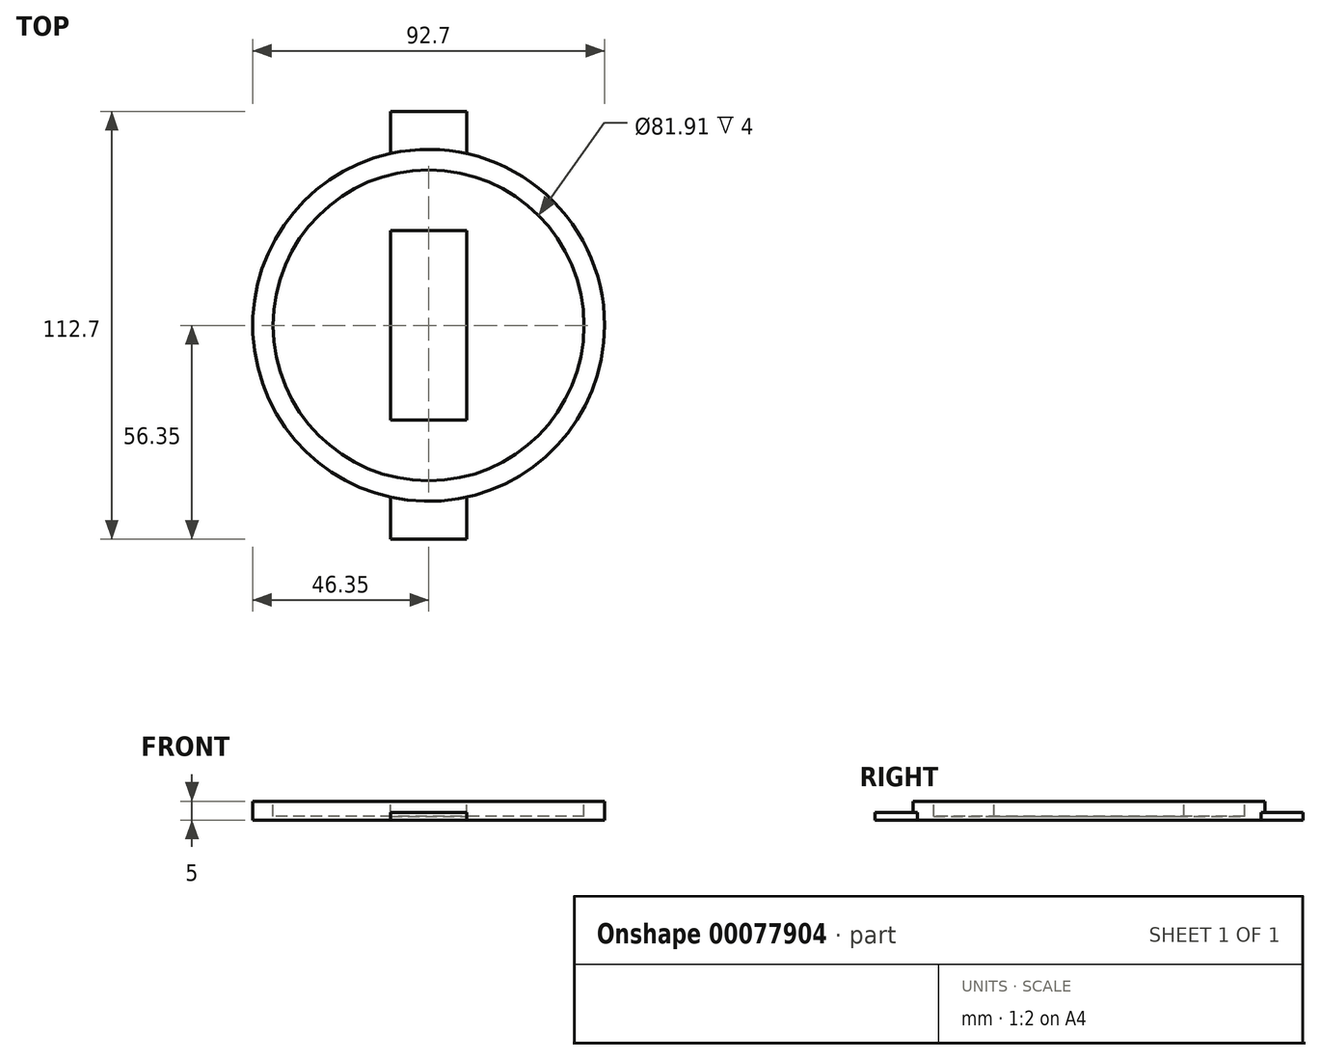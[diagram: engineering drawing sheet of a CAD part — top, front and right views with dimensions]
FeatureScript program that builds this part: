
annotation { "Feature Type Name" : "Feature", "Feature Type Description" : "" }
export const myFeature = defineFeature(function(context is Context, id is Id, definition is map)
    precondition{}
    {
        {
            var Q0;
            Q0=qCreatedBy(makeId("Top.planeOp"),FACE);
            var sketch = newSketch(context, id + "F0", { "sketchPlane" : qUnion([Q0])});
            skCircle(sketch, "E0", {"center": v(0, 0) * mm, "radius": 46.35 * mm});
            skLineSegment(sketch, "E1.bottom", {"start": v(60, -60) * mm, "end": v(-60, -60) * mm});
            skLineSegment(sketch, "E1.top", {"start": v(60, 60) * mm, "end": v(-60, 60) * mm});
            skLineSegment(sketch, "E1.left", {"start": v(60, -60) * mm, "end": v(60, 60) * mm});
            skLineSegment(sketch, "E1.right", {"start": v(-60, -60) * mm, "end": v(-60, 60) * mm});
            skSolve(sketch);
        }
        {
            var Q0;
            Q0=makeQuery(id+"F0.imprint","IMPRINT",FACE,{"disambiguationData":[TD([[makeQuery(id+"F0.imprint","IMPRINT",EDGE,{"derivedFrom":sQuery(id+"F0.wireOp",EDGE,"E0")}),1.0]])]});
            var Q1;
            Q1=makeQuery(id+"F0.imprint","IMPRINT",FACE,{"disambiguationData":[TD([[makeQuery(id+"F0.imprint","IMPRINT",EDGE,{"derivedFrom":sQuery(id+"F0.wireOp",EDGE,"da6a9297-29b8-4a20-b414-be6ac6d7b623.bottom")}),1.0]])]});
            extrude(context, id + "F1", {"entities" : qUnion([Q0, Q1]), "depth" : 5 * mm});
        }
        {
            var Q0;
            Q0=makeQuery(id+"F1.opExtrude","CAP_FACE",FACE,{"disambiguationData":[OSD([sQuery(id+"F0.wireOp",EDGE,"E0")])],"isStart":false});
            var sketch = newSketch(context, id + "F2", { "sketchPlane" : qUnion([Q0])});
            skLineSegment(sketch, "E2.bottom", {"start": v(-10, -25) * mm, "end": v(10, -25) * mm});
            skLineSegment(sketch, "E2.top", {"start": v(-10, 25) * mm, "end": v(10, 25) * mm});
            skLineSegment(sketch, "E2.left", {"start": v(-10, -25) * mm, "end": v(-10, 25) * mm});
            skLineSegment(sketch, "E2.right", {"start": v(10, -25) * mm, "end": v(10, 25) * mm});
            skPoint(sketch, "E2.middle", {"position": v(0, 0) * mm});
            skCircle(sketch, "E3", {"center": v(0, 0) * mm, "radius": 40.95 * mm});
            skSolve(sketch);
        }
        {
            var Q0;
            Q0=makeQuery(id+"F2.imprint","IMPRINT",FACE,{"disambiguationData":[TD([[makeQuery(id+"F2.imprint","IMPRINT",EDGE,{"derivedFrom":sQuery(id+"F2.wireOp",EDGE,"E2.bottom")}),-1.0]])]});
            extrude(context, id + "F3", {"entities" : qUnion([Q0]), "operationType" : NewBodyOperationType.REMOVE, "oppositeDirection" : true, "depth" : 4 * mm});
        }
        {
            var Q0;
            Q0=makeQuery(id+"F0.imprint","IMPRINT",FACE,{"disambiguationData":[TD([[makeQuery(id+"F0.imprint","IMPRINT",EDGE,{"derivedFrom":sQuery(id+"F0.wireOp",EDGE,"E0")}),1.0]])]});
            var sketch = newSketch(context, id + "F4", { "sketchPlane" : qUnion([Q0])});
            skLineSegment(sketch, "E4", {"start": v(10, 56.35) * mm, "end": v(0, 56.35) * mm});
            skLineSegment(sketch, "E5", {"start": v(-10, 56.35) * mm, "end": v(-10, 39.74) * mm});
            skLineSegment(sketch, "E6", {"start": v(0, 56.35) * mm, "end": v(-10, 56.35) * mm});
            skLineSegment(sketch, "E7", {"start": v(10, 38.42) * mm, "end": v(10, 56.35) * mm});
            skLineSegment(sketch, "E8", {"start": v(10, -40.85) * mm, "end": v(10, -56.35) * mm});
            skLineSegment(sketch, "E9", {"start": v(10, -56.35) * mm, "end": v(-10, -56.35) * mm});
            skLineSegment(sketch, "E10", {"start": v(-10, -56.35) * mm, "end": v(-10, -40.94) * mm});
            skSolve(sketch);
        }
        {
            var Q0;
            {var subQ0=sQuery(id+"F4.wireOp",EDGE,"E4");Q0=makeQuery(id+"F4.imprint","IMPRINT",FACE,{"disambiguationData":[TD([[makeQuery(id+"F4.imprint","IMPRINT",EDGE,{"derivedFrom":subQ0}),1.0]])]});}
            extrude(context, id + "F5", {"entities" : qUnion([Q0]), "operationType" : NewBodyOperationType.ADD, "depth" : 2 * mm});
        }
        {
            var Q0;
            {var subQ0=sQuery(id+"F4.wireOp",EDGE,"E9");Q0=makeQuery(id+"F4.imprint","IMPRINT",FACE,{"disambiguationData":[TD([[makeQuery(id+"F4.imprint","IMPRINT",EDGE,{"derivedFrom":subQ0}),-1.0]])]});}
            extrude(context, id + "F6", {"entities" : qUnion([Q0]), "operationType" : NewBodyOperationType.ADD, "depth" : 2 * mm});
        }
    });
